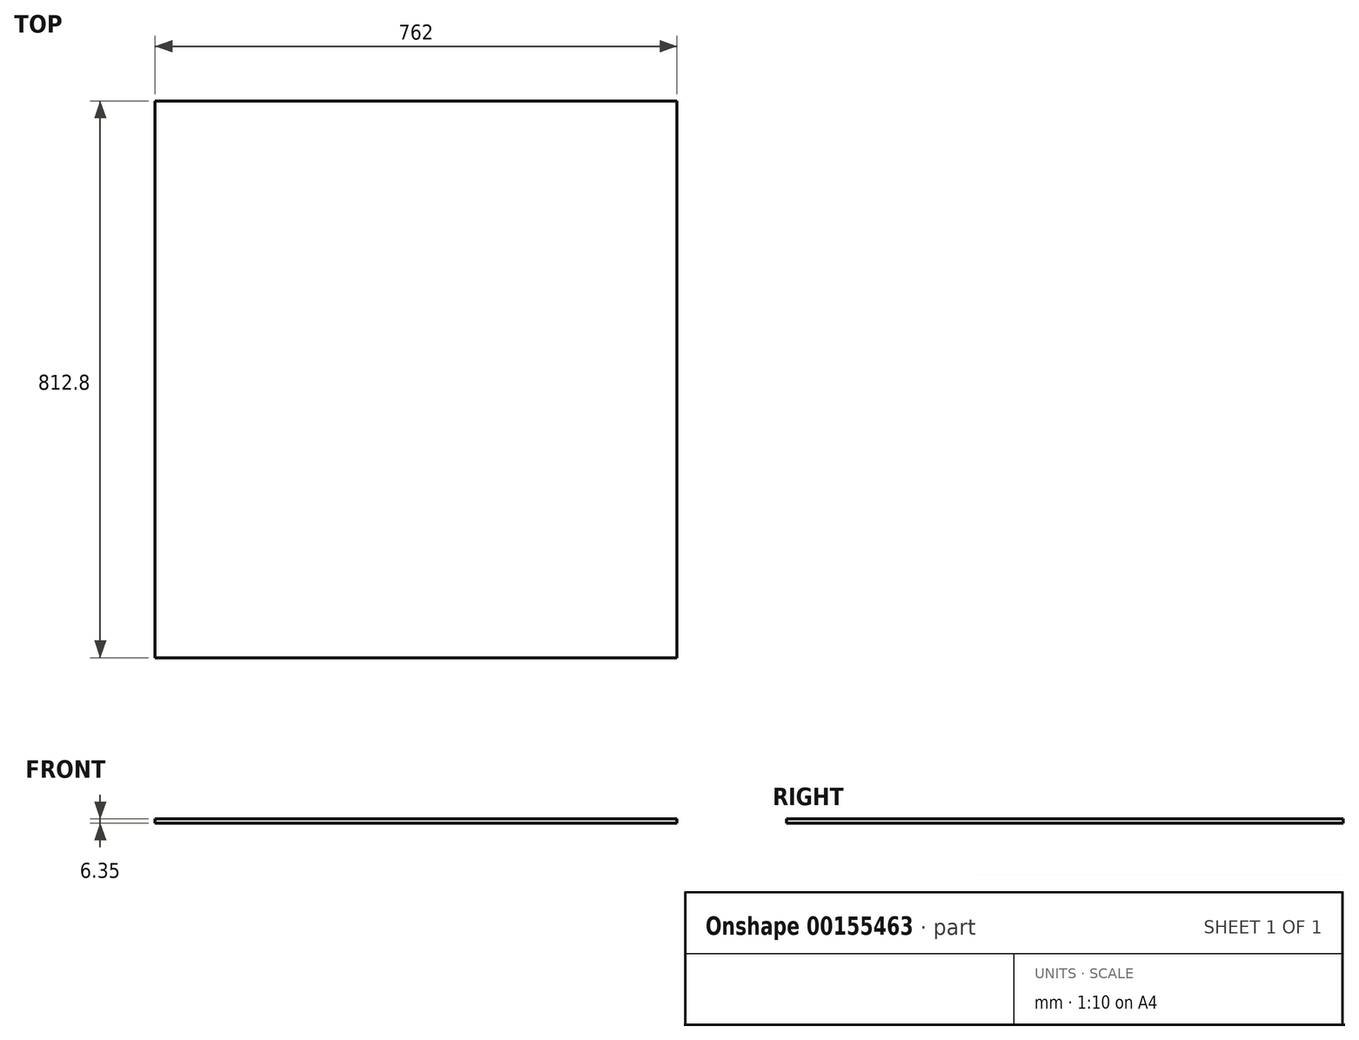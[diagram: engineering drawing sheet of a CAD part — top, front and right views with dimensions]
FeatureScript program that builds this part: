
annotation { "Feature Type Name" : "Feature", "Feature Type Description" : "" }
export const myFeature = defineFeature(function(context is Context, id is Id, definition is map)
    precondition{}
    {
        {
            var Q0;
            Q0=qCreatedBy(makeId("Top.planeOp"),FACE);
            var sketch = newSketch(context, id + "F0", { "sketchPlane" : qUnion([Q0])});
            skLineSegment(sketch, "E0.bottom", {"start": v(0, 0) * mm, "end": v(762, 0) * mm});
            skLineSegment(sketch, "E0.top", {"start": v(0, 812.8) * mm, "end": v(762, 812.8) * mm});
            skLineSegment(sketch, "E0.left", {"start": v(0, 0) * mm, "end": v(0, 812.8) * mm});
            skLineSegment(sketch, "E0.right", {"start": v(762, 0) * mm, "end": v(762, 812.8) * mm});
            skSolve(sketch);
        }
        {
            var Q0;
            Q0 = qSketchRegion(id + "F0", true);
            extrude(context, id + "F1", {"entities" : qUnion([Q0]), "depth" : 6.35 * mm});
        }
    });
